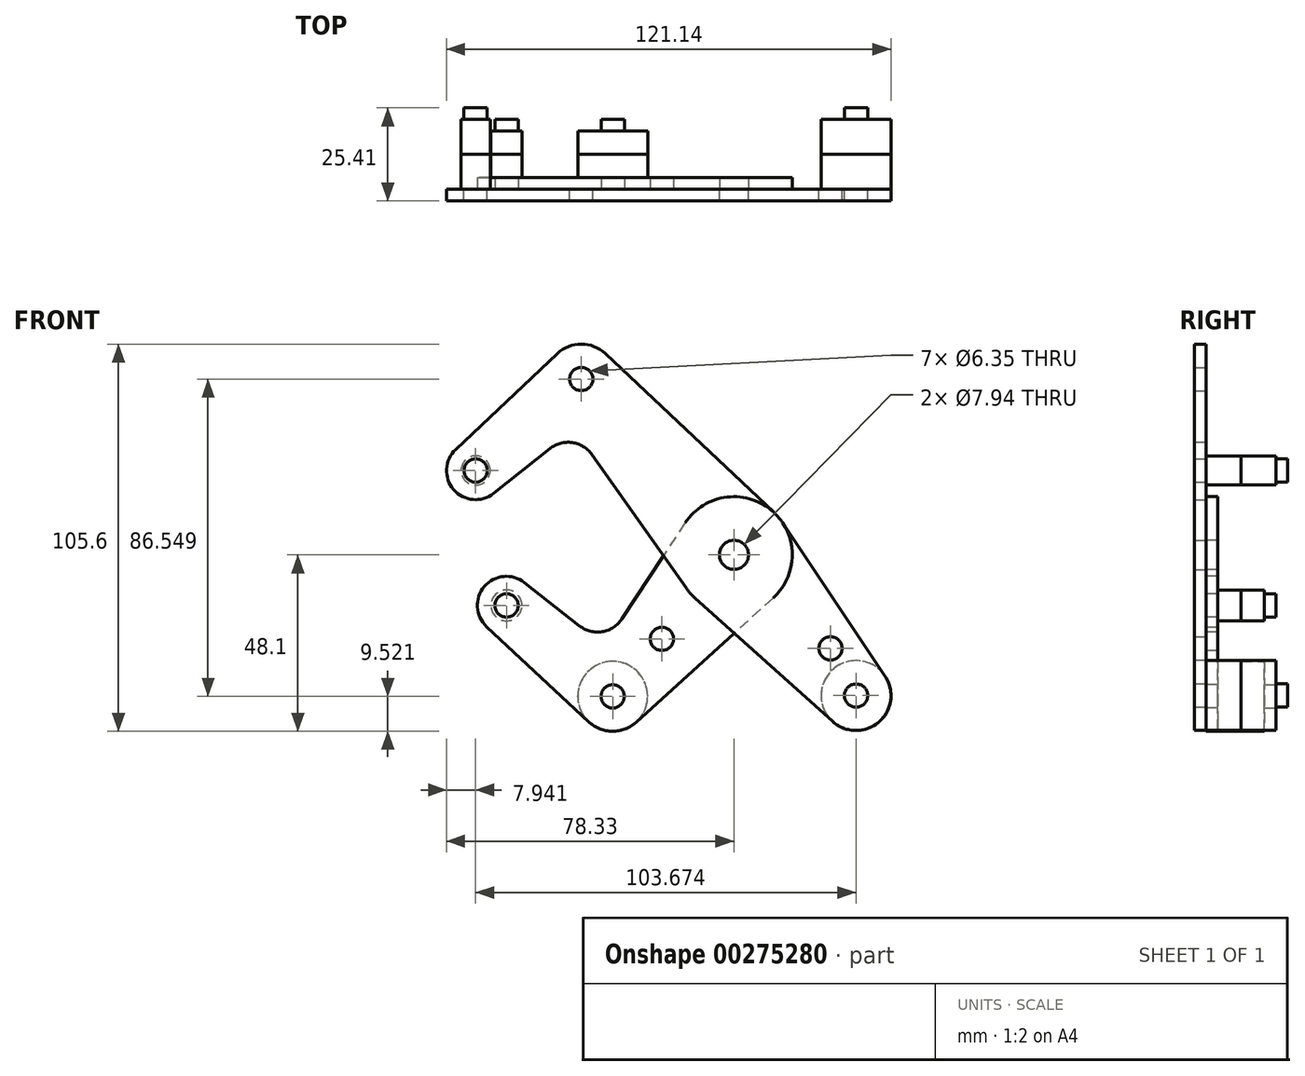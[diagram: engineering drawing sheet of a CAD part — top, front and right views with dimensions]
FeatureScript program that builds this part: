
annotation { "Feature Type Name" : "Feature", "Feature Type Description" : "" }
export const myFeature = defineFeature(function(context is Context, id is Id, definition is map)
    precondition{}
    {
        {
            var Q0;
            Q0=qCreatedBy(makeId("Front.planeOp"),FACE);
            var sketch = newSketch(context, id + "F0", { "sketchPlane" : qUnion([Q0])});
            skLineSegment(sketch, "E0", {"start": v(-41.6, 47.97) * mm, "end": v(41.6, -47.97) * mm, "construction": true});
            skCircle(sketch, "E1", {"center": v(0, 0) * mm, "radius": 3.18 * mm});
            skCircle(sketch, "E2", {"center": v(33.29, -38.38) * mm, "radius": 3.18 * mm});
            skCircle(sketch, "E3", {"center": v(-41.6, 47.97) * mm, "radius": 3.18 * mm});
            skCircle(sketch, "E4", {"center": v(-70.39, 23) * mm, "radius": 3.18 * mm});
            skLineSegment(sketch, "E5", {"start": v(-41.6, 47.97) * mm, "end": v(-70.39, 23) * mm, "construction": true});
            skCircle(sketch, "E6", {"center": v(33.29, -38.38) * mm, "radius": 9.53 * mm});
            skCircle(sketch, "E7", {"center": v(-70.39, 23) * mm, "radius": 7.94 * mm});
            skCircle(sketch, "E8", {"center": v(-41.6, 47.97) * mm, "radius": 9.53 * mm});
            skLineSegment(sketch, "E9", {"start": v(-75.83, 28.78) * mm, "end": v(-48.14, 54.9) * mm});
            skLineSegment(sketch, "E10", {"start": v(-65.44, 16.8) * mm, "end": v(-50.15, 28.98) * mm});
            skCircle(sketch, "E11", {"center": v(0, 0) * mm, "radius": 15.88 * mm});
            skLineSegment(sketch, "E12", {"start": v(-35.07, 54.9) * mm, "end": v(10.9, 11.55) * mm});
            skLineSegment(sketch, "E13", {"start": v(-38.72, 27.35) * mm, "end": v(-12.97, -9.15) * mm});
            skLineSegment(sketch, "E14", {"start": v(-10.6, -11.82) * mm, "end": v(26.93, -45.47) * mm});
            skLineSegment(sketch, "E15", {"start": v(13.2, 8.82) * mm, "end": v(41.2, -33.08) * mm});
            skArc(sketch, "E16.filletArc", {"start": v(-38.72, 27.35) * mm, "mid": v(-44.08, 30.63) * mm, "end": v(-50.15, 28.98) * mm});
            skLineSegment(sketch, "E17", {"start": v(0, 0) * mm, "end": v(-33.05, -38.58) * mm, "construction": true});
            skLineSegment(sketch, "E18", {"start": v(-33.05, -38.58) * mm, "end": v(-61.98, -13.8) * mm, "construction": true});
            skCircle(sketch, "E19", {"center": v(-61.98, -13.8) * mm, "radius": 3.18 * mm});
            skCircle(sketch, "E20", {"center": v(-33.05, -38.58) * mm, "radius": 3.18 * mm});
            skCircle(sketch, "E21", {"center": v(-61.98, -13.8) * mm, "radius": 7.94 * mm});
            skCircle(sketch, "E22", {"center": v(-33.05, -38.58) * mm, "radius": 9.53 * mm});
            skLineSegment(sketch, "E23", {"start": v(-57.08, -7.55) * mm, "end": v(-42.08, -19.35) * mm});
            skLineSegment(sketch, "E24", {"start": v(-67.4, -19.6) * mm, "end": v(-39.54, -45.55) * mm});
            skLineSegment(sketch, "E25", {"start": v(-13.25, 8.74) * mm, "end": v(-30.55, -17.48) * mm});
            skLineSegment(sketch, "E26", {"start": v(10.67, -11.75) * mm, "end": v(-26.65, -45.63) * mm});
            skArc(sketch, "E27.filletArc", {"start": v(-42.08, -19.35) * mm, "mid": v(-35.9, -20.95) * mm, "end": v(-30.55, -17.48) * mm});
            skCircle(sketch, "E28", {"center": v(-19.62, -22.9) * mm, "radius": 3.18 * mm});
            skCircle(sketch, "E29", {"center": v(26.32, -25.5) * mm, "radius": 3.18 * mm});
            skLineSegment(sketch, "E30", {"start": v(26.32, -25.5) * mm, "end": v(23.92, -27.58) * mm, "construction": true});
            skCircle(sketch, "E31", {"center": v(0, 0) * mm, "radius": 3.97 * mm});
            skSolve(sketch);
        }
        {
            var Q0;
            Q0=qCreatedBy(makeId("Front.planeOp"),FACE);
            cPlane(context, id + "F1", {"entities" : qUnion([Q0]), "cplaneType" : CPlaneType.OFFSET, "offset" : 9.52 * mm, "oppositeDirection" : true, "width" : 254 * mm, "height" : 254 * mm});
        }
        {
            var Q0;
            Q0=makeQuery(id+"F0.imprint","IMPRINT",FACE,{"disambiguationData":[TD([[makeQuery(id+"F0.imprint","IMPRINT",EDGE,{"derivedFrom":sQuery(id+"F0.wireOp",EDGE,"E2")}),-1.0]])]});
            var Q1;
            Q1=makeQuery(id+"F0.imprint","IMPRINT",FACE,{"disambiguationData":[TD([[makeQuery(id+"F0.imprint","IMPRINT",EDGE,{"derivedFrom":sQuery(id+"F0.wireOp",EDGE,"E3")}),-1.0]])]});
            var Q2;
            Q2=makeQuery(id+"F0.imprint","IMPRINT",FACE,{"disambiguationData":[TD([[makeQuery(id+"F0.imprint","IMPRINT",EDGE,{"derivedFrom":sQuery(id+"F0.wireOp",EDGE,"E4")}),-1.0]])]});
            var Q3;
            {var subQ0=sQuery(id+"F0.wireOp",EDGE,"E13");var subQ1=sQuery(id+"F0.wireOp",EDGE,"E11");var subQ2=makeQuery(id+"F0.imprint","INTERSECT",VERTEX,{"derivedFrom":[subQ1,subQ0]});Q3=makeQuery(id+"F0.imprint","IMPRINT",FACE,{"disambiguationData":[TD([[makeQuery(id+"F0.imprint","IMPRINT",EDGE,{"disambiguationData":[TD([[subQ2,1.0]])],"derivedFrom":subQ1}),-1.0]])]});}
            var Q4;
            {var subQ0=sQuery(id+"F0.wireOp",EDGE,"E14");var subQ1=sQuery(id+"F0.wireOp",EDGE,"E11");var subQ2=makeQuery(id+"F0.imprint","INTERSECT",VERTEX,{"derivedFrom":[subQ1,subQ0]});Q4=makeQuery(id+"F0.imprint","IMPRINT",FACE,{"disambiguationData":[TD([[makeQuery(id+"F0.imprint","IMPRINT",EDGE,{"disambiguationData":[TD([[subQ2,-1.0]])],"derivedFrom":subQ1}),-1.0]])]});}
            var Q5;
            {var subQ0=sQuery(id+"F0.wireOp",EDGE,"E15");Q5=makeQuery(id+"F0.imprint","IMPRINT",FACE,{"disambiguationData":[TD([[makeQuery(id+"F0.imprint","IMPRINT",EDGE,{"derivedFrom":subQ0}),-1.0]])]});}
            var Q6;
            {var subQ1=sQuery(id+"F0.wireOp",EDGE,"E9");Q6=makeQuery(id+"F0.imprint","IMPRINT",FACE,{"disambiguationData":[TD([[makeQuery(id+"F0.imprint","IMPRINT",EDGE,{"derivedFrom":subQ1}),-1.0]])]});}
            var Q7;
            Q7=makeQuery(id+"F0.imprint","IMPRINT",FACE,{"disambiguationData":[TD([[makeQuery(id+"F0.imprint","IMPRINT",EDGE,{"derivedFrom":sQuery(id+"F0.wireOp",EDGE,"E31")}),-1.0]])]});
            extrude(context, id + "F2", {"entities" : qUnion([Q0, Q1, Q2, Q3, Q4, Q5, Q6, Q7]), "depth" : 3.17 * mm});
        }
        {
            var Q0;
            Q0=makeQuery(id+"F0.imprint","IMPRINT",FACE,{"disambiguationData":[TD([[makeQuery(id+"F0.imprint","IMPRINT",EDGE,{"derivedFrom":sQuery(id+"F0.wireOp",EDGE,"E20")}),-1.0]])]});
            var Q1;
            Q1=makeQuery(id+"F0.imprint","IMPRINT",FACE,{"disambiguationData":[TD([[makeQuery(id+"F0.imprint","IMPRINT",EDGE,{"derivedFrom":sQuery(id+"F0.wireOp",EDGE,"E19")}),-1.0]])]});
            var Q2;
            {var subQ0=sQuery(id+"F0.wireOp",EDGE,"E13");var subQ1=sQuery(id+"F0.wireOp",EDGE,"E11");var subQ2=makeQuery(id+"F0.imprint","INTERSECT",VERTEX,{"derivedFrom":[subQ1,subQ0]});Q2=makeQuery(id+"F0.imprint","IMPRINT",FACE,{"disambiguationData":[TD([[makeQuery(id+"F0.imprint","IMPRINT",EDGE,{"disambiguationData":[TD([[subQ2,1.0]])],"derivedFrom":subQ1}),-1.0]])]});}
            var Q3;
            {var subQ0=sQuery(id+"F0.wireOp",EDGE,"E14");var subQ1=sQuery(id+"F0.wireOp",EDGE,"E11");var subQ2=makeQuery(id+"F0.imprint","INTERSECT",VERTEX,{"derivedFrom":[subQ1,subQ0]});Q3=makeQuery(id+"F0.imprint","IMPRINT",FACE,{"disambiguationData":[TD([[makeQuery(id+"F0.imprint","IMPRINT",EDGE,{"disambiguationData":[TD([[subQ2,-1.0]])],"derivedFrom":subQ1}),-1.0]])]});}
            var Q4;
            {var subQ10=sQuery(id+"F0.wireOp",EDGE,"E23");Q4=makeQuery(id+"F0.imprint","IMPRINT",FACE,{"disambiguationData":[TD([[makeQuery(id+"F0.imprint","IMPRINT",EDGE,{"derivedFrom":subQ10}),-1.0]])]});}
            var Q5;
            Q5=makeQuery(id+"F0.imprint","IMPRINT",FACE,{"disambiguationData":[TD([[makeQuery(id+"F0.imprint","IMPRINT",EDGE,{"derivedFrom":sQuery(id+"F0.wireOp",EDGE,"E31")}),-1.0]])]});
            extrude(context, id + "F3", {"entities" : qUnion([Q0, Q1, Q2, Q3, Q4, Q5]), "oppositeDirection" : true, "depth" : 3.17 * mm});
        }
        {
            var Q0;
            Q0=makeQuery(id+"F2.opExtrude","CAP_FACE",FACE,{"disambiguationData":[OSD([sQuery(id+"F0.wireOp",EDGE,"E2"),sQuery(id+"F0.wireOp",EDGE,"E3"),sQuery(id+"F0.wireOp",EDGE,"E4"),sQuery(id+"F0.wireOp",EDGE,"E6"),sQuery(id+"F0.wireOp",EDGE,"E7"),sQuery(id+"F0.wireOp",EDGE,"E8"),sQuery(id+"F0.wireOp",EDGE,"E9"),sQuery(id+"F0.wireOp",EDGE,"E10"),sQuery(id+"F0.wireOp",EDGE,"E11"),sQuery(id+"F0.wireOp",EDGE,"E12"),sQuery(id+"F0.wireOp",EDGE,"E13"),sQuery(id+"F0.wireOp",EDGE,"E14"),sQuery(id+"F0.wireOp",EDGE,"E15"),sQuery(id+"F0.wireOp",EDGE,"E16.filletArc"),sQuery(id+"F0.wireOp",EDGE,"E29"),sQuery(id+"F0.wireOp",EDGE,"E31")])],"isStart":false});
            var sketch = newSketch(context, id + "F4", { "sketchPlane" : qUnion([Q0])});
            skCircle(sketch, "E32", {"center": v(-70.39, 23) * mm, "radius": 3.98 * mm});
            skCircle(sketch, "E33", {"center": v(33.29, -38.38) * mm, "radius": 9.53 * mm});
            skSolve(sketch);
        }
        {
            var Q0;
            Q0=makeQuery(id+"F3.opExtrude","CAP_FACE",FACE,{"disambiguationData":[OSD([sQuery(id+"F0.wireOp",EDGE,"E11"),sQuery(id+"F0.wireOp",EDGE,"E19"),sQuery(id+"F0.wireOp",EDGE,"E20"),sQuery(id+"F0.wireOp",EDGE,"E21"),sQuery(id+"F0.wireOp",EDGE,"E22"),sQuery(id+"F0.wireOp",EDGE,"E23"),sQuery(id+"F0.wireOp",EDGE,"E24"),sQuery(id+"F0.wireOp",EDGE,"E25"),sQuery(id+"F0.wireOp",EDGE,"E26"),sQuery(id+"F0.wireOp",EDGE,"E27.filletArc"),sQuery(id+"F0.wireOp",EDGE,"E28"),sQuery(id+"F0.wireOp",EDGE,"E31")])],"isStart":true});
            var sketch = newSketch(context, id + "F5", { "sketchPlane" : qUnion([Q0])});
            skCircle(sketch, "E34", {"center": v(-33.05, -38.58) * mm, "radius": 9.53 * mm});
            skCircle(sketch, "E35", {"center": v(-61.98, -13.8) * mm, "radius": 4.22 * mm});
            skSolve(sketch);
        }
        {
            var Q0;
            Q0 = qSketchRegion(id + "F4", true);
            var Q1;
            Q1 = qSketchRegion(id + "F5", true);
            var Q2;
            Q2=qCreatedBy(id+"F1.planeOp",FACE);
            extrude(context, id + "F6", {"entities" : qUnion([Q0, Q1]), "endBound" : BoundingType.UP_TO_SURFACE, "oppositeDirection" : true, "endBoundEntityFace" : qUnion([Q2]), "depth" : 25.4 * mm});
        }
        {
            var Q0;
            Q0=makeQuery(id+"F2.opExtrude","SWEPT_BODY",BODY,{"disambiguationData":[OSD([sQuery(id+"F0.wireOp",EDGE,"E2"),sQuery(id+"F0.wireOp",EDGE,"E3"),sQuery(id+"F0.wireOp",EDGE,"E4"),sQuery(id+"F0.wireOp",EDGE,"E6"),sQuery(id+"F0.wireOp",EDGE,"E7"),sQuery(id+"F0.wireOp",EDGE,"E8"),sQuery(id+"F0.wireOp",EDGE,"E9"),sQuery(id+"F0.wireOp",EDGE,"E10"),sQuery(id+"F0.wireOp",EDGE,"E11"),sQuery(id+"F0.wireOp",EDGE,"E12"),sQuery(id+"F0.wireOp",EDGE,"E13"),sQuery(id+"F0.wireOp",EDGE,"E14"),sQuery(id+"F0.wireOp",EDGE,"E15"),sQuery(id+"F0.wireOp",EDGE,"E16.filletArc"),sQuery(id+"F0.wireOp",EDGE,"E29"),sQuery(id+"F0.wireOp",EDGE,"E31")])]});
            var Q1;
            Q1=makeQuery(id+"F3.opExtrude","SWEPT_BODY",BODY,{"disambiguationData":[OSD([sQuery(id+"F0.wireOp",EDGE,"E11"),sQuery(id+"F0.wireOp",EDGE,"E19"),sQuery(id+"F0.wireOp",EDGE,"E20"),sQuery(id+"F0.wireOp",EDGE,"E21"),sQuery(id+"F0.wireOp",EDGE,"E22"),sQuery(id+"F0.wireOp",EDGE,"E23"),sQuery(id+"F0.wireOp",EDGE,"E24"),sQuery(id+"F0.wireOp",EDGE,"E25"),sQuery(id+"F0.wireOp",EDGE,"E26"),sQuery(id+"F0.wireOp",EDGE,"E27.filletArc"),sQuery(id+"F0.wireOp",EDGE,"E28"),sQuery(id+"F0.wireOp",EDGE,"E31")])]});
            var Q2;
            Q2=makeQuery(id+"F6.opExtrude","SWEPT_BODY",BODY,{"disambiguationData":[OSD([sQuery(id+"F4.wireOp",EDGE,"E32")])]});
            var Q3;
            Q3=makeQuery(id+"F6.opExtrude","SWEPT_BODY",BODY,{"disambiguationData":[OSD([sQuery(id+"F5.wireOp",EDGE,"E35")])]});
            var Q4;
            Q4=makeQuery(id+"F6.opExtrude","SWEPT_BODY",BODY,{"disambiguationData":[OSD([sQuery(id+"F5.wireOp",EDGE,"E34")])]});
            var Q5;
            Q5=makeQuery(id+"F6.opExtrude","SWEPT_BODY",BODY,{"disambiguationData":[OSD([sQuery(id+"F4.wireOp",EDGE,"E33")])]});
            booleanBodies(context, id + "F7", {"operationType" : BooleanOperationType.SUBTRACTION, "tools" : qUnion([Q0, Q1]), "targets" : qUnion([Q2, Q3, Q4, Q5]), "keepTools" : true});
        }
        {
            var Q0;
            Q0=makeQuery(id+"F6.opExtrude","SWEPT_BODY",BODY,{"disambiguationData":[OSD([sQuery(id+"F4.wireOp",EDGE,"E32")])]});
            var Q1;
            Q1=makeQuery(id+"F6.opExtrude","SWEPT_BODY",BODY,{"disambiguationData":[OSD([sQuery(id+"F5.wireOp",EDGE,"E35")])]});
            var Q2;
            Q2=makeQuery(id+"F6.opExtrude","SWEPT_BODY",BODY,{"disambiguationData":[OSD([sQuery(id+"F5.wireOp",EDGE,"E34")])]});
            var Q3;
            Q3=makeQuery(id+"F6.opExtrude","SWEPT_BODY",BODY,{"disambiguationData":[OSD([sQuery(id+"F4.wireOp",EDGE,"E33")])]});
            var Q4;
            Q4=qCreatedBy(id+"F1.planeOp",FACE);
            mirror(context, id + "F8", {"entities" : qUnion([Q0, Q1, Q2, Q3]), "mirrorPlane" : qUnion([Q4])});
        }
    });
